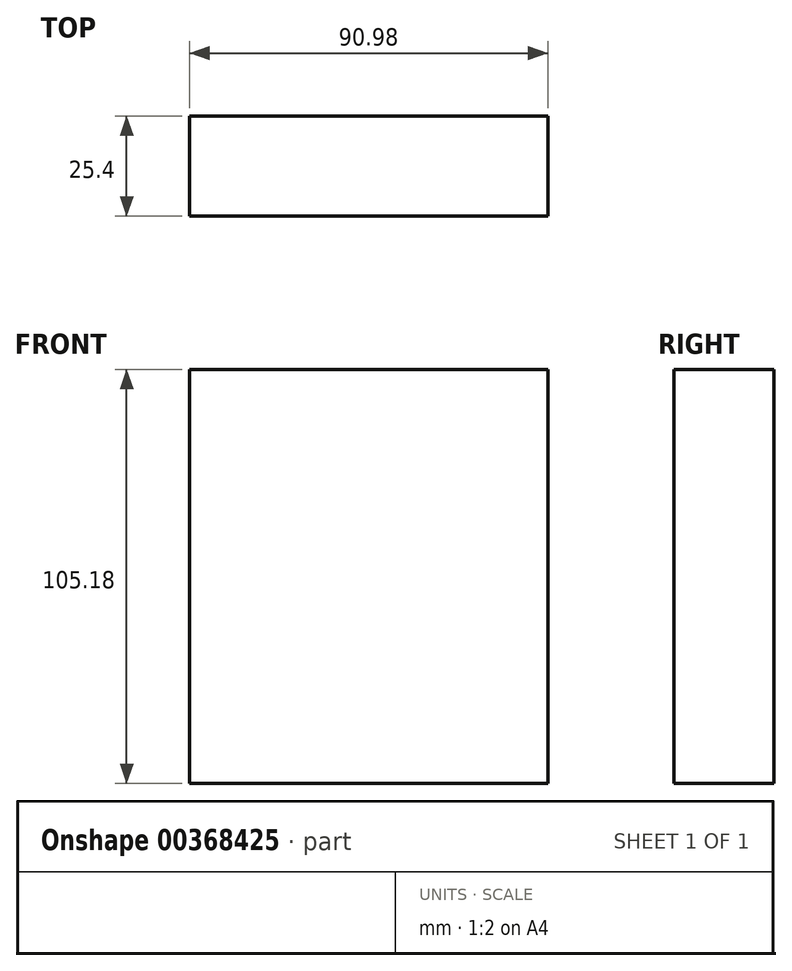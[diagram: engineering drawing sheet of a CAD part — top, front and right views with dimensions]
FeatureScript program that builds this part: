
annotation { "Feature Type Name" : "Feature", "Feature Type Description" : "" }
export const myFeature = defineFeature(function(context is Context, id is Id, definition is map)
    precondition{}
    {
        {
            var Q0;
            Q0=qCreatedBy(makeId("Front.planeOp"),FACE);
            var sketch = newSketch(context, id + "F0", { "sketchPlane" : qUnion([Q0])});
            skLineSegment(sketch, "E0.bottom", {"start": v(87.49, -53.47) * mm, "end": v(-3.49, -53.47) * mm});
            skLineSegment(sketch, "E0.top", {"start": v(87.49, 51.7) * mm, "end": v(-3.49, 51.7) * mm});
            skLineSegment(sketch, "E0.left", {"start": v(87.49, -53.47) * mm, "end": v(87.49, 51.7) * mm});
            skLineSegment(sketch, "E0.right", {"start": v(-3.49, -53.47) * mm, "end": v(-3.49, 51.7) * mm});
            skSolve(sketch);
        }
        {
            var Q0;
            Q0 = qSketchRegion(id + "F0", true);
            extrude(context, id + "F1", {"entities" : qUnion([Q0]), "depth" : 25.4 * mm});
        }
    });
